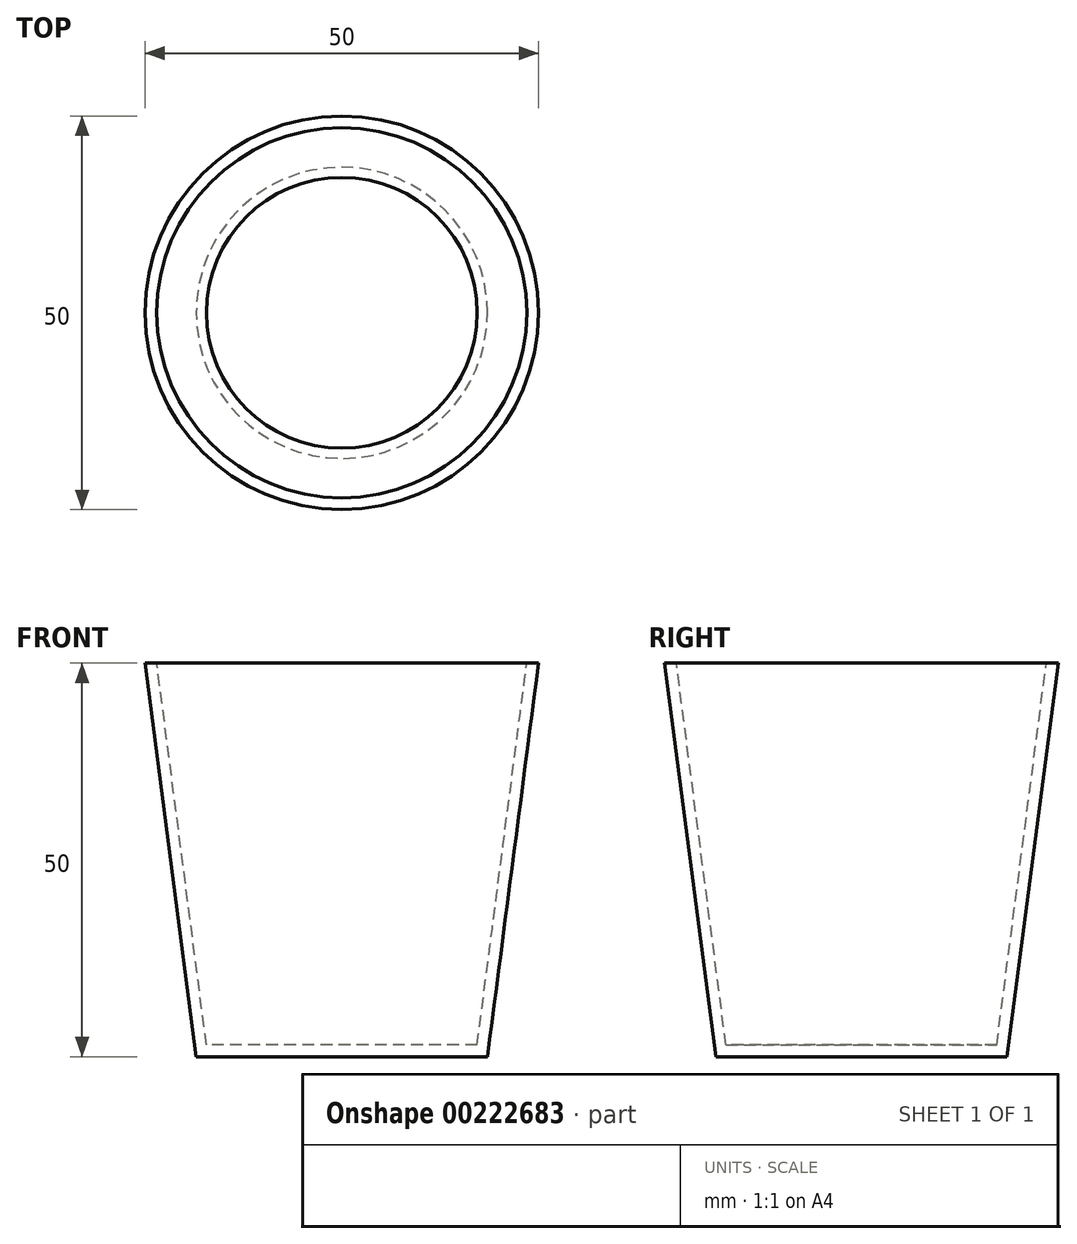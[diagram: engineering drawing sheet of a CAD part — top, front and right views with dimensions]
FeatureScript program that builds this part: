
annotation { "Feature Type Name" : "Feature", "Feature Type Description" : "" }
export const myFeature = defineFeature(function(context is Context, id is Id, definition is map)
    precondition{}
    {
        {
            var Q0;
            Q0=qCreatedBy(makeId("Top.planeOp"),FACE);
            var sketch = newSketch(context, id + "F0", { "sketchPlane" : qUnion([Q0])});
            skCircle(sketch, "E0", {"center": v(0, 0) * mm, "radius": 25 * mm});
            skCircle(sketch, "E1", {"center": v(0, 0) * mm, "radius": 23.5 * mm});
            skSolve(sketch);
        }
        {
            var Q0;
            Q0=qCreatedBy(makeId("Right.planeOp"),FACE);
            var sketch = newSketch(context, id + "F1", { "sketchPlane" : qUnion([Q0])});
            skLineSegment(sketch, "E2", {"start": v(0, 0) * mm, "end": v(0, -50) * mm, "construction": true});
            skLineSegment(sketch, "E3", {"start": v(15.16, -50) * mm, "end": v(-15.16, -50) * mm, "construction": true});
            skSolve(sketch);
        }
        {
            var Q0;
            Q0=sQuery(id+"F1.wireOp",EDGE,"E3");
            cPlane(context, id + "F2", {"entities" : qUnion([Q0]), "cplaneType" : CPlaneType.LINE_ANGLE, "offset" : 25 * mm, "angle" : 0 * degree, "width" : 150 * mm, "height" : 150 * mm});
        }
        {
            var Q0;
            Q0=qCreatedBy(id+"F2.planeOp",FACE);
            var sketch = newSketch(context, id + "F3", { "sketchPlane" : qUnion([Q0])});
            skCircle(sketch, "E4", {"center": v(0, 0) * mm, "radius": 18.5 * mm});
            skCircle(sketch, "E5", {"center": v(0, 0) * mm, "radius": 17 * mm});
            skSolve(sketch);
        }
        {
            var Q0;
            Q0=qCreatedBy(makeId("Right.planeOp"),FACE);
            var sketch = newSketch(context, id + "F4", { "sketchPlane" : qUnion([Q0])});
            skLineSegment(sketch, "E6.0", {"start": v(-25, 0) * mm, "end": v(25, 0) * mm});
            skLineSegment(sketch, "E7.0", {"start": v(18.5, -50) * mm, "end": v(-18.5, -50) * mm});
            skLineSegment(sketch, "E8", {"start": v(18.5, -50) * mm, "end": v(25, 0) * mm});
            skLineSegment(sketch, "E9", {"start": v(17.2, -48.5) * mm, "end": v(23.5, 0) * mm});
            skLineSegment(sketch, "E10", {"start": v(17.2, -48.5) * mm, "end": v(0, -48.5) * mm});
            skLineSegment(sketch, "E11", {"start": v(0, -48.5) * mm, "end": v(0, -50) * mm});
            skSolve(sketch);
        }
        {
            var Q0;
            {var subQ1=sQuery(id+"F4.wireOp",EDGE,"E8");Q0=makeQuery(id+"F4.imprint","IMPRINT",FACE,{"disambiguationData":[TD([[makeQuery(id+"F4.imprint","IMPRINT",EDGE,{"derivedFrom":subQ1}),1.0]])]});}
            var Q1;
            Q1=sQuery(id+"F1.wireOp",EDGE,"E2");
            revolve(context, id + "F5", {"entities" : qUnion([Q0]), "axis" : qUnion([Q1]), "revolveType" : RevolveType.FULL});
        }
    });
